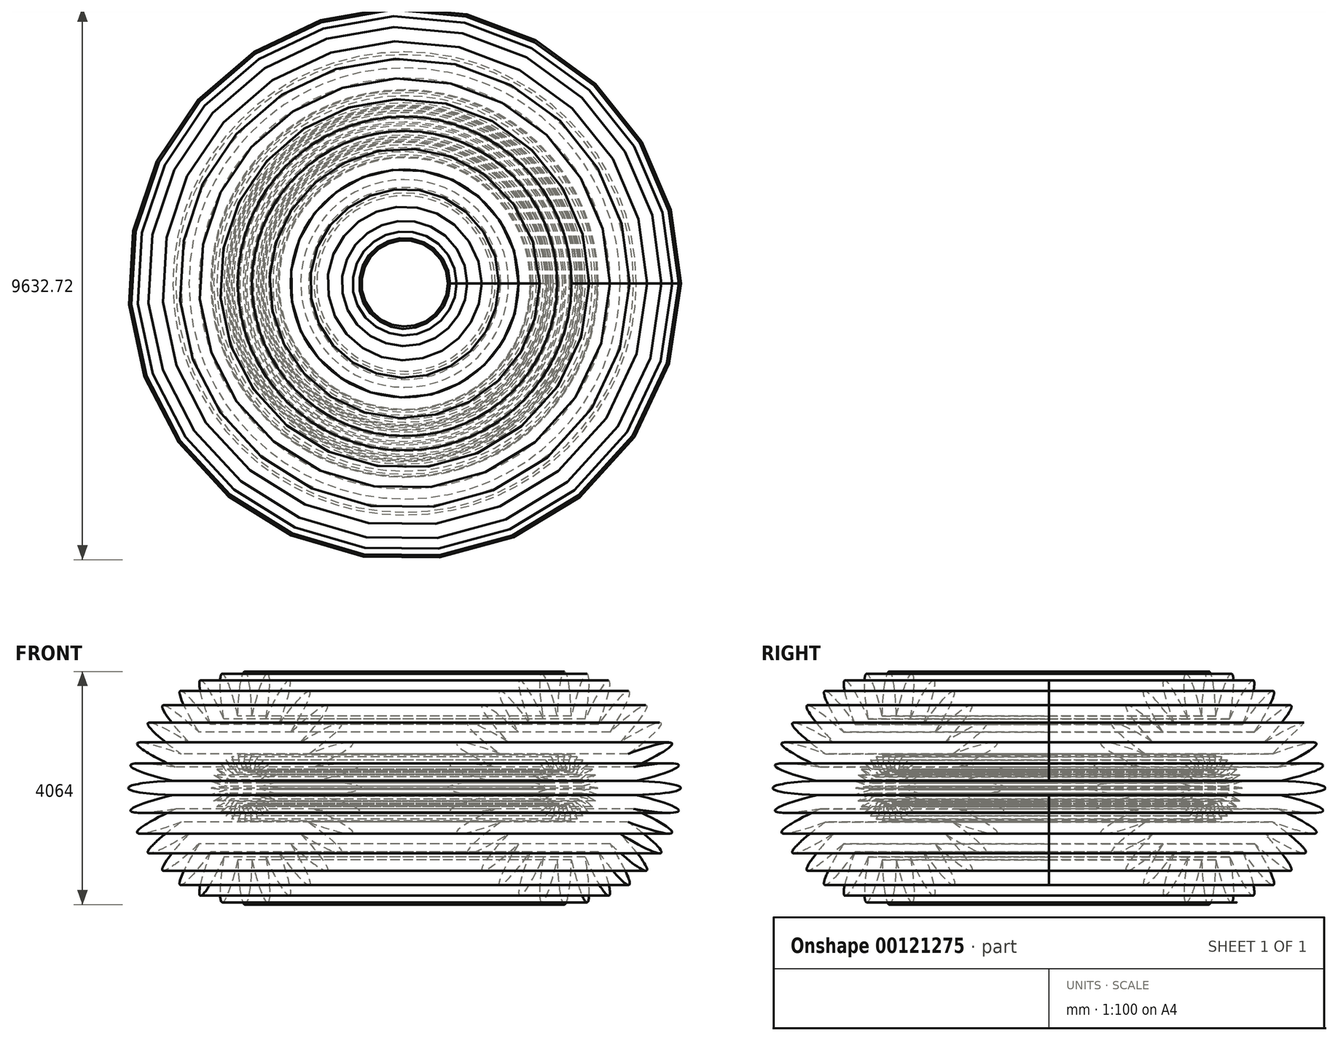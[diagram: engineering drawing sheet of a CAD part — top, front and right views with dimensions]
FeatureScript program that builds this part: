
annotation { "Feature Type Name" : "Feature", "Feature Type Description" : "" }
export const myFeature = defineFeature(function(context is Context, id is Id, definition is map)
    precondition{}
    {
        {
            var Q0;
            Q0=qCreatedBy(makeId("Front.planeOp"),FACE);
            var sketch = newSketch(context, id + "F0", { "sketchPlane" : qUnion([Q0])});
            skCircle(sketch, "E0", {"center": v(0, 0) * mm, "radius": 127 * mm});
            skEllipse(sketch, "E1", {"center": v(-564.46, 844.77) * mm, "majorRadius": 1016 * mm, "minorRadius": 127 * mm, "majorAxis": v(0.56, -0.83)});
            skEllipse(sketch, "E2", {"center": v(-388.8, 938.66) * mm, "majorRadius": 1016 * mm, "minorRadius": 127 * mm, "majorAxis": v(0.38, -0.92)});
            skEllipse(sketch, "E3.MirrorC", {"center": v(0, 1016) * mm, "majorRadius": 1016 * mm, "minorRadius": 127 * mm, "majorAxis": v(0, -1)});
            skEllipse(sketch, "E4.MirrorC", {"center": v(198.21, 996.48) * mm, "majorRadius": 1016 * mm, "minorRadius": 127 * mm, "majorAxis": v(-0.2, -0.98)});
            skEllipse(sketch, "E5.MirrorC", {"center": v(388.8, 938.66) * mm, "majorRadius": 1016 * mm, "minorRadius": 127 * mm, "majorAxis": v(-0.38, -0.92)});
            skEllipse(sketch, "E6.MirrorC", {"center": v(564.46, 844.77) * mm, "majorRadius": 1016 * mm, "minorRadius": 127 * mm, "majorAxis": v(-0.56, -0.83)});
            skEllipse(sketch, "E7.MirrorC", {"center": v(-198.21, 996.48) * mm, "majorRadius": 1016 * mm, "minorRadius": 127 * mm, "majorAxis": v(0.2, -0.98)});
            skEllipse(sketch, "E8.MirrorC", {"center": v(-938.66, 388.8) * mm, "majorRadius": 1016 * mm, "minorRadius": 127 * mm, "majorAxis": v(0.92, -0.38)});
            skEllipse(sketch, "E9.MirrorC", {"center": v(-844.77, 564.46) * mm, "majorRadius": 1016 * mm, "minorRadius": 127 * mm, "majorAxis": v(0.83, -0.56)});
            skEllipse(sketch, "E10.MirrorC", {"center": v(-996.48, 198.21) * mm, "majorRadius": 1016 * mm, "minorRadius": 127 * mm, "majorAxis": v(0.98, -0.2)});
            skEllipse(sketch, "E11.MirrorC", {"center": v(-1016, 0) * mm, "majorRadius": 1016 * mm, "minorRadius": 127 * mm, "majorAxis": v(1, 0)});
            skEllipse(sketch, "E12.MirrorC", {"center": v(-718.42, 718.42) * mm, "majorRadius": 1016 * mm, "minorRadius": 127 * mm, "majorAxis": v(0.7, -0.7)});
            skEllipse(sketch, "E13.MirrorC", {"center": v(-564.46, -844.77) * mm, "majorRadius": 1016 * mm, "minorRadius": 127 * mm, "majorAxis": v(0.56, 0.83)});
            skEllipse(sketch, "E14.MirrorC", {"center": v(-718.42, -718.42) * mm, "majorRadius": 1016 * mm, "minorRadius": 127 * mm, "majorAxis": v(0.7, 0.7)});
            skEllipse(sketch, "E15.MirrorC", {"center": v(-844.77, -564.46) * mm, "majorRadius": 1016 * mm, "minorRadius": 127 * mm, "majorAxis": v(0.83, 0.56)});
            skEllipse(sketch, "E16.MirrorC", {"center": v(-938.66, -388.8) * mm, "majorRadius": 1016 * mm, "minorRadius": 127 * mm, "majorAxis": v(0.92, 0.38)});
            skEllipse(sketch, "E17.MirrorC", {"center": v(-996.48, -198.21) * mm, "majorRadius": 1016 * mm, "minorRadius": 127 * mm, "majorAxis": v(0.98, 0.2)});
            skEllipse(sketch, "E18.MirrorC", {"center": v(564.46, -844.77) * mm, "majorRadius": 1016 * mm, "minorRadius": 127 * mm, "majorAxis": v(-0.56, 0.83)});
            skEllipse(sketch, "E19.MirrorC", {"center": v(388.8, -938.66) * mm, "majorRadius": 1016 * mm, "minorRadius": 127 * mm, "majorAxis": v(-0.38, 0.92)});
            skEllipse(sketch, "E20.MirrorC", {"center": v(198.21, -996.48) * mm, "majorRadius": 1016 * mm, "minorRadius": 127 * mm, "majorAxis": v(-0.2, 0.98)});
            skEllipse(sketch, "E21.MirrorC", {"center": v(-388.8, -938.66) * mm, "majorRadius": 1016 * mm, "minorRadius": 127 * mm, "majorAxis": v(0.38, 0.92)});
            skEllipse(sketch, "E22.MirrorC", {"center": v(-198.21, -996.48) * mm, "majorRadius": 1016 * mm, "minorRadius": 127 * mm, "majorAxis": v(0.2, 0.98)});
            skEllipse(sketch, "E23.MirrorC", {"center": v(0, -1016) * mm, "majorRadius": 1016 * mm, "minorRadius": 127 * mm, "majorAxis": v(0, 1)});
            skEllipse(sketch, "E24.MirrorC", {"center": v(718.42, -718.42) * mm, "majorRadius": 1016 * mm, "minorRadius": 127 * mm, "majorAxis": v(-0.7, 0.7)});
            skEllipse(sketch, "E25.MirrorC", {"center": v(844.77, -564.46) * mm, "majorRadius": 1016 * mm, "minorRadius": 127 * mm, "majorAxis": v(-0.83, 0.56)});
            skEllipse(sketch, "E26.MirrorC", {"center": v(938.66, -388.8) * mm, "majorRadius": 1016 * mm, "minorRadius": 127 * mm, "majorAxis": v(-0.92, 0.38)});
            skEllipse(sketch, "E27.MirrorC", {"center": v(996.48, -198.21) * mm, "majorRadius": 1016 * mm, "minorRadius": 127 * mm, "majorAxis": v(-0.98, 0.2)});
            skEllipse(sketch, "E28.MirrorC", {"center": v(1016, 0) * mm, "majorRadius": 1016 * mm, "minorRadius": 127 * mm, "majorAxis": v(-1, 0)});
            skEllipse(sketch, "E29.MirrorC", {"center": v(996.48, 198.21) * mm, "majorRadius": 1016 * mm, "minorRadius": 127 * mm, "majorAxis": v(-0.98, -0.2)});
            skEllipse(sketch, "E30.MirrorC", {"center": v(938.66, 388.8) * mm, "majorRadius": 1016 * mm, "minorRadius": 127 * mm, "majorAxis": v(-0.92, -0.38)});
            skEllipse(sketch, "E31.MirrorC", {"center": v(844.77, 564.46) * mm, "majorRadius": 1016 * mm, "minorRadius": 127 * mm, "majorAxis": v(-0.83, -0.56)});
            skEllipse(sketch, "E32.MirrorC", {"center": v(718.42, 718.42) * mm, "majorRadius": 1016 * mm, "minorRadius": 127 * mm, "majorAxis": v(-0.7, -0.7)});
            skLineSegment(sketch, "E33", {"start": v(-2784.36, 1094.72) * mm, "end": v(-2784.36, -2345.65) * mm});
            skSolve(sketch);
        }
        {
            var Q0;
            Q0 = qSketchRegion(id + "F0", true);
            var Q1;
            Q1=sQuery(id+"F0.wireOp",EDGE,"E33");
            revolve(context, id + "F1", {"entities" : qUnion([Q0]), "axis" : qUnion([Q1]), "revolveType" : RevolveType.FULL});
        }
    });
